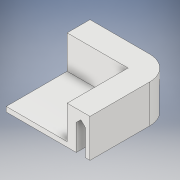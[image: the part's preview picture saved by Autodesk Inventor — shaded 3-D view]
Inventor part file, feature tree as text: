
AUTODESK INVENTOR PART (.ipt)
format: ipt  version: 2019 (Build 230136000, 136)  size: 137,728 bytes
history: native  units: in
note: dims shown in document units (in); Inventor stores cm internally (conversion verified against a paired STEP export)
features: extrude x3, sketch x3, fillet x1, chamfer x1
ambient origin geometry x8: Origin, YZ Plane, XZ Plane, XY Plane, X Axis, Y Axis, Z Axis, Center Point
bodies: Solid1 (feature_tree)
feature tree (8):
  extrude  "Extrusion1"  Depth=0.375in
  extrude  "Extrusion2"  Depth=0.375in
  fillet  "Fillet1"  Radius=0.375in
  chamfer  "Chamfer1"  Distance=0.625in
  extrude  "Extrusion3"  Depth=0.3in
  sketch  "Sketch1"  dims[d0=0.375in d1=0.375in]
  sketch  "Sketch2"  dims[d2=1.0in d3=0.375in d4=0.375in]
  sketch  "Sketch3"  dims[d5=1.0in d6=0.625in d7=0.0in d8=0.3in d9=0.3in d10=0.15in d11=1.3in d12=1.3in d13=0.15in d14=0.5in d15=0.0in d16=0.3937in d17=0.0725in d18=0.125in d19=45.0deg d20=1.0in d21=1.0in d22=0.0787in d23=0.0in]
